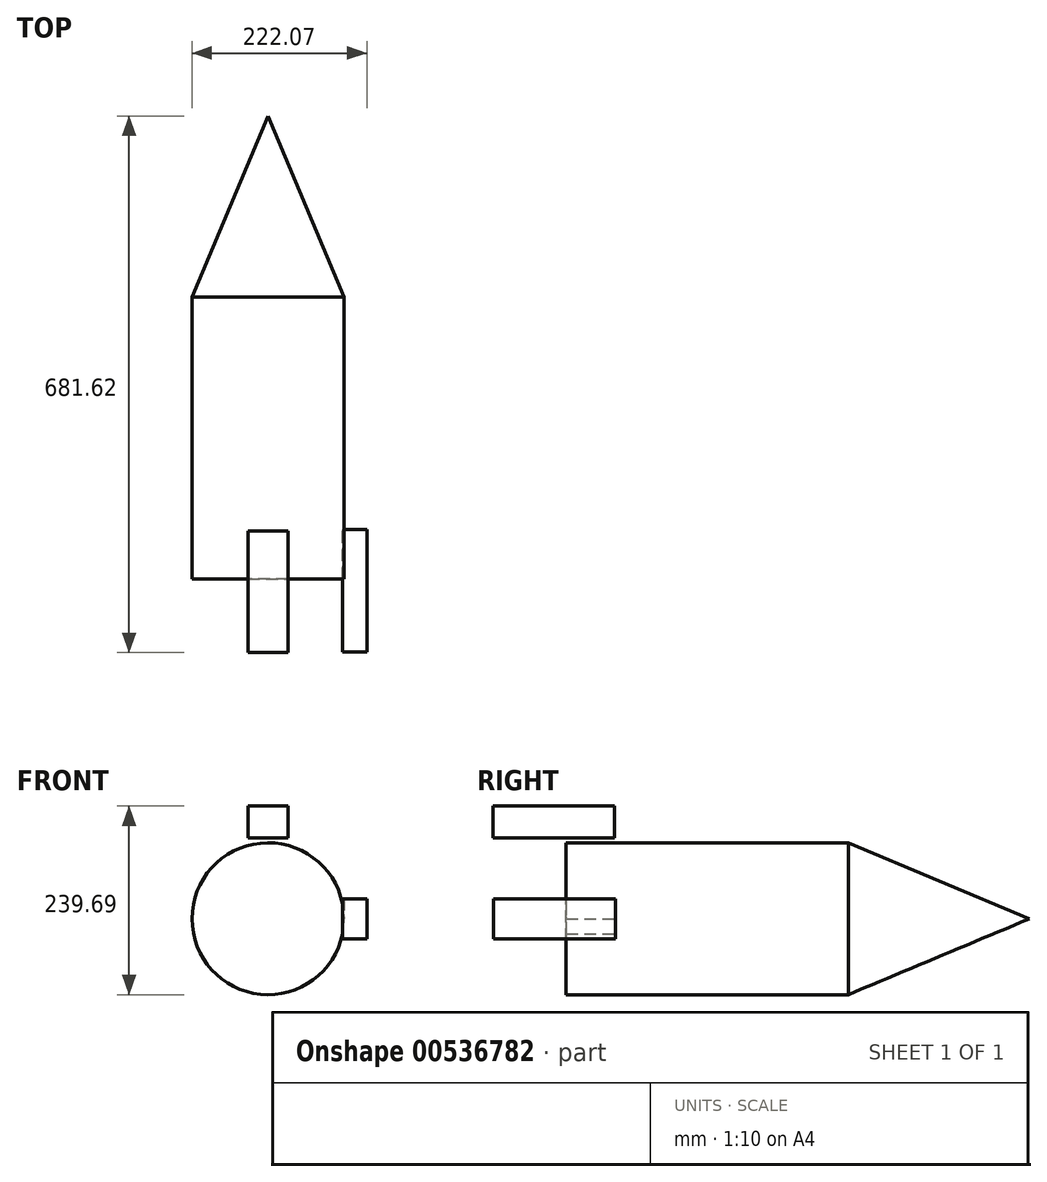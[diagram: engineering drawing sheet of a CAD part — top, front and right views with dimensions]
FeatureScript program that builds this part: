
annotation { "Feature Type Name" : "Feature", "Feature Type Description" : "" }
export const myFeature = defineFeature(function(context is Context, id is Id, definition is map)
    precondition{}
    {
        {
            var Q0;
            Q0=qCreatedBy(makeId("Front.planeOp"),FACE);
            var sketch = newSketch(context, id + "F0", { "sketchPlane" : qUnion([Q0])});
            skCircle(sketch, "E0", {"center": v(0, 0) * mm, "radius": 96.47 * mm});
            skSolve(sketch);
        }
        {
            var Q0;
            Q0=qCreatedBy(makeId("Right.planeOp"),FACE);
            var sketch = newSketch(context, id + "F1", { "sketchPlane" : qUnion([Q0])});
            skCircle(sketch, "E1", {"center": v(0, 0) * mm, "radius": 95.7 * mm});
            skSolve(sketch);
        }
        {
            var Q0;
            Q0 = qSketchRegion(id + "F1", true);
            var sketch = newSketch(context, id + "F2", { "sketchPlane" : qUnion([Q0])});
            skSolve(sketch);
        }
        {
            var Q0;
            Q0=makeQuery(id+"F0.imprint","IMPRINT",FACE,{"disambiguationData":[TD([[makeQuery(id+"F0.imprint","IMPRINT",EDGE,{"derivedFrom":sQuery(id+"F0.wireOp",EDGE,"E0")}),1.0]])]});
            var sketch = newSketch(context, id + "F3", { "sketchPlane" : qUnion([Q0])});
            skLineSegment(sketch, "E2.0", {"start": v(-96.74, 0) * mm, "end": v(96.74, 0) * mm});
            skLineSegment(sketch, "E3.0", {"start": v(0, 95.7) * mm, "end": v(0, -95.7) * mm});
            skCircle(sketch, "E4.0", {"center": v(0, 0) * mm, "radius": 96.47 * mm});
            skSolve(sketch);
        }
        {
            var Q0;
            {var subQ0=sQuery(id+"F3.wireOp",EDGE,"E2.0");var subQ4=makeQuery(id+"F3.imprint","IMPRINT",VERTEX,{"derivedFrom":subQ0});Q0=makeQuery(id+"F3.imprint","IMPRINT",FACE,{"disambiguationData":[TD([[makeQuery(id+"F3.imprint","IMPRINT",EDGE,{"disambiguationData":[TD([[subQ4,1.0]])],"derivedFrom":subQ0}),1.0]])]});}
            extrude(context, id + "F4", {"entities" : qUnion([Q0]), "depth" : 356.8 * mm, "offsetDistance" : 25.4 * mm});
        }
        {
            var Q0;
            Q0=makeQuery(id+"F0.imprint","IMPRINT",FACE,{"disambiguationData":[TD([[makeQuery(id+"F0.imprint","IMPRINT",EDGE,{"derivedFrom":sQuery(id+"F0.wireOp",EDGE,"E0")}),1.0]])]});
            extrude(context, id + "F5", {"entities" : qUnion([Q0]), "operationType" : NewBodyOperationType.ADD, "depth" : 358.33 * mm, "offsetDistance" : 25.4 * mm});
        }
        {
            var Q0;
            Q0=makeQuery(id+"F2.imprint","IMPRINT",FACE,{"disambiguationData":[TD([[makeQuery(id+"F2.imprint","IMPRINT",EDGE,{"derivedFrom":makeQuery(id+"F1.imprint","IMPRINT",EDGE,{"derivedFrom":sQuery(id+"F1.wireOp",EDGE,"E1")})}),1.0]])]});
            var sketch = newSketch(context, id + "F6", { "sketchPlane" : qUnion([Q0])});
            skPoint(sketch, "E5", {"position": v(95.47, 0) * mm});
            skSolve(sketch);
        }
        {
            var Q0;
            Q0=qCreatedBy(makeId("Top.planeOp"),FACE);
            var sketch = newSketch(context, id + "F7", { "sketchPlane" : qUnion([Q0])});
            skLineSegment(sketch, "E6.bottom", {"start": v(-94.58, -295.46) * mm, "end": v(-125.6, -295.46) * mm});
            skLineSegment(sketch, "E6.top", {"start": v(-94.58, -450.8) * mm, "end": v(-125.6, -450.8) * mm});
            skLineSegment(sketch, "E6.left", {"start": v(-94.58, -295.46) * mm, "end": v(-94.58, -450.8) * mm});
            skLineSegment(sketch, "E6.right", {"start": v(-125.6, -295.46) * mm, "end": v(-125.6, -450.8) * mm});
            skLineSegment(sketch, "E7.bottom", {"start": v(98.15, -294.89) * mm, "end": v(134.1, -294.89) * mm});
            skLineSegment(sketch, "E7.top", {"start": v(98.15, -453.69) * mm, "end": v(134.1, -453.69) * mm});
            skLineSegment(sketch, "E7.left", {"start": v(98.15, -294.89) * mm, "end": v(98.15, -453.69) * mm});
            skLineSegment(sketch, "E7.right", {"start": v(134.1, -294.89) * mm, "end": v(134.1, -453.69) * mm});
            skSolve(sketch);
        }
        {
            var Q0;
            Q0=qCreatedBy(makeId("Right.planeOp"),FACE);
            var sketch = newSketch(context, id + "F8", { "sketchPlane" : qUnion([Q0])});
            skLineSegment(sketch, "E8.bottom", {"start": v(-297.08, -100.02) * mm, "end": v(-452.27, -100.02) * mm});
            skLineSegment(sketch, "E8.top", {"start": v(-297.08, -139.5) * mm, "end": v(-452.27, -139.5) * mm});
            skLineSegment(sketch, "E8.left", {"start": v(-297.08, -100.02) * mm, "end": v(-297.08, -139.5) * mm});
            skLineSegment(sketch, "E8.right", {"start": v(-452.27, -100.02) * mm, "end": v(-452.27, -139.5) * mm});
            skLineSegment(sketch, "E9.bottom", {"start": v(-297.08, 102.68) * mm, "end": v(-451.49, 102.68) * mm});
            skLineSegment(sketch, "E9.top", {"start": v(-297.08, 143.22) * mm, "end": v(-451.49, 143.22) * mm});
            skLineSegment(sketch, "E9.left", {"start": v(-297.08, 102.68) * mm, "end": v(-297.08, 143.22) * mm});
            skLineSegment(sketch, "E9.right", {"start": v(-451.49, 102.68) * mm, "end": v(-451.49, 143.22) * mm});
            skSolve(sketch);
        }
        {
            var Q0;
            Q0=makeQuery(id+"F7.imprint","IMPRINT",FACE,{"disambiguationData":[TD([[makeQuery(id+"F7.imprint","IMPRINT",EDGE,{"derivedFrom":sQuery(id+"F7.wireOp",EDGE,"E6.bottom")}),1.0]])]});
            extrude(context, id + "F9", {"entities" : qUnion([Q0]), "operationType" : NewBodyOperationType.ADD, "oppositeDirection" : true, "depth" : 25.4 * mm, "offsetDistance" : 25.4 * mm});
        }
        {
            var Q0;
            Q0=makeQuery(id+"F9.opExtrude","CAP_FACE",FACE,{"disambiguationData":[OSD([sQuery(id+"F7.wireOp",EDGE,"E6.bottom"),sQuery(id+"F7.wireOp",EDGE,"E6.top"),sQuery(id+"F7.wireOp",EDGE,"E6.left"),sQuery(id+"F7.wireOp",EDGE,"E6.right")])],"isStart":true});
            extrude(context, id + "F10", {"entities" : qUnion([Q0]), "operationType" : NewBodyOperationType.ADD, "depth" : 25.4 * mm, "offsetDistance" : 25.4 * mm});
        }
        {
            var Q0;
            Q0=makeQuery(id+"F8.imprint","IMPRINT",FACE,{"disambiguationData":[TD([[makeQuery(id+"F8.imprint","IMPRINT",EDGE,{"derivedFrom":sQuery(id+"F8.wireOp",EDGE,"E8.bottom")}),1.0]])]});
            extrude(context, id + "F11", {"entities" : qUnion([Q0]), "oppositeDirection" : true, "depth" : 25.4 * mm, "offsetDistance" : 25.4 * mm});
        }
        {
            var Q0;
            Q0=makeQuery(id+"F11.opExtrude","CAP_FACE",FACE,{"disambiguationData":[OSD([sQuery(id+"F8.wireOp",EDGE,"E8.bottom"),sQuery(id+"F8.wireOp",EDGE,"E8.top"),sQuery(id+"F8.wireOp",EDGE,"E8.left"),sQuery(id+"F8.wireOp",EDGE,"E8.right")])],"isStart":true});
            extrude(context, id + "F12", {"entities" : qUnion([Q0]), "operationType" : NewBodyOperationType.ADD, "depth" : 25.4 * mm, "offsetDistance" : 25.4 * mm});
        }
        {
            var Q0;
            Q0=makeQuery(id+"F7.imprint","IMPRINT",FACE,{"disambiguationData":[TD([[makeQuery(id+"F7.imprint","IMPRINT",EDGE,{"derivedFrom":sQuery(id+"F7.wireOp",EDGE,"E7.bottom")}),-1.0]])]});
            extrude(context, id + "F13", {"entities" : qUnion([Q0]), "depth" : 25.4 * mm, "offsetDistance" : 25.4 * mm});
        }
        {
            var Q0;
            Q0=makeQuery(id+"F7.imprint","IMPRINT",FACE,{"disambiguationData":[TD([[makeQuery(id+"F7.imprint","IMPRINT",EDGE,{"derivedFrom":sQuery(id+"F7.wireOp",EDGE,"E7.bottom")}),-1.0]])]});
            extrude(context, id + "F14", {"entities" : qUnion([Q0]), "operationType" : NewBodyOperationType.ADD, "depth" : 25.4 * mm, "offsetDistance" : 25.4 * mm});
        }
        {
            var Q0;
            Q0=makeQuery(id+"F7.imprint","IMPRINT",FACE,{"disambiguationData":[TD([[makeQuery(id+"F7.imprint","IMPRINT",EDGE,{"derivedFrom":sQuery(id+"F7.wireOp",EDGE,"E7.bottom")}),-1.0]])]});
            extrude(context, id + "F15", {"entities" : qUnion([Q0]), "operationType" : NewBodyOperationType.ADD, "oppositeDirection" : true, "depth" : 25.4 * mm, "offsetDistance" : 25.4 * mm});
        }
        {
            var Q0;
            Q0=makeQuery(id+"F8.imprint","IMPRINT",FACE,{"disambiguationData":[TD([[makeQuery(id+"F8.imprint","IMPRINT",EDGE,{"derivedFrom":sQuery(id+"F8.wireOp",EDGE,"E9.bottom")}),-1.0]])]});
            extrude(context, id + "F16", {"entities" : qUnion([Q0]), "depth" : 25.4 * mm, "offsetDistance" : 25.4 * mm});
        }
        {
            var Q0;
            Q0=makeQuery(id+"F8.imprint","IMPRINT",FACE,{"disambiguationData":[TD([[makeQuery(id+"F8.imprint","IMPRINT",EDGE,{"derivedFrom":sQuery(id+"F8.wireOp",EDGE,"E9.bottom")}),-1.0]])]});
            extrude(context, id + "F17", {"entities" : qUnion([Q0]), "operationType" : NewBodyOperationType.ADD, "oppositeDirection" : true, "depth" : 25.4 * mm, "offsetDistance" : 25.4 * mm});
        }
        {
            var Q0;
            Q0=qCreatedBy(makeId("Top.planeOp"),FACE);
            var sketch = newSketch(context, id + "F18", { "sketchPlane" : qUnion([Q0])});
            skPoint(sketch, "E10", {"position": v(0, 230.13) * mm});
            skSolve(sketch);
        }
        {
            var Q0;
            Q0=sQuery(id+"F18.wireOp",VERTEX,"E10");
            var Q1;
            Q1=makeQuery(id+"F5.boolean.opBoolean","MERGE",FACE,{"derivedFrom":[makeQuery(id+"F4.opExtrude","CAP_FACE",FACE,{"disambiguationData":[OSD([sQuery(id+"F3.wireOp",EDGE,"E4.0"),sQuery(id+"F3.wireOp",EDGE,"E2.0")])],"isStart":true}),makeQuery(id+"F5.opExtrude","CAP_FACE",FACE,{"disambiguationData":[OSD([sQuery(id+"F0.wireOp",EDGE,"E0")])],"isStart":true})]});
            loft(context, id + "F19", {"sheetProfilesArray" : [{ "sheetProfileEntities" : qUnion([Q0]) }, { "sheetProfileEntities" : qUnion([Q1]) }]});
        }
        {
            var Q0;
            Q0=makeQuery(id+"F4.opExtrude","SWEPT_BODY",BODY,{"disambiguationData":[OSD([sQuery(id+"F3.wireOp",EDGE,"E4.0"),sQuery(id+"F3.wireOp",EDGE,"E2.0")])]});
            var Q1;
            Q1=makeQuery(id+"F6.imprint","IMPRINT",FACE,{"disambiguationData":[TD([[makeQuery(id+"F6.imprint","IMPRINT",EDGE,{"derivedFrom":makeQuery(id+"F2.imprint","IMPRINT",EDGE,{"derivedFrom":makeQuery(id+"F1.imprint","IMPRINT",EDGE,{"derivedFrom":sQuery(id+"F1.wireOp",EDGE,"E1")})})}),1.0]])]});
            mirror(context, id + "F20", {"entities" : qUnion([Q0]), "mirrorPlane" : qUnion([Q1])});
        }
        {
            var Q0;
            Q0=makeQuery(id+"F11.opExtrude","SWEPT_BODY",BODY,{"disambiguationData":[OSD([sQuery(id+"F8.wireOp",EDGE,"E8.bottom"),sQuery(id+"F8.wireOp",EDGE,"E8.top"),sQuery(id+"F8.wireOp",EDGE,"E8.left"),sQuery(id+"F8.wireOp",EDGE,"E8.right")])]});
            var Q1;
            Q1=makeQuery(id+"F4.opExtrude","SWEPT_BODY",BODY,{"disambiguationData":[OSD([sQuery(id+"F3.wireOp",EDGE,"E4.0"),sQuery(id+"F3.wireOp",EDGE,"E2.0")])]});
            deleteBodies(context, id + "F21", {"entities" : qUnion([Q0, Q1])});
        }
        {
            var Q0;
            Q0=makeQuery(id+"F13.opExtrude","SWEPT_BODY",BODY,{"disambiguationData":[OSD([sQuery(id+"F7.wireOp",EDGE,"E7.bottom"),sQuery(id+"F7.wireOp",EDGE,"E7.top"),sQuery(id+"F7.wireOp",EDGE,"E7.left"),sQuery(id+"F7.wireOp",EDGE,"E7.right")])]});
            deleteBodies(context, id + "F22", {"entities" : qUnion([Q0])});
        }
    });
